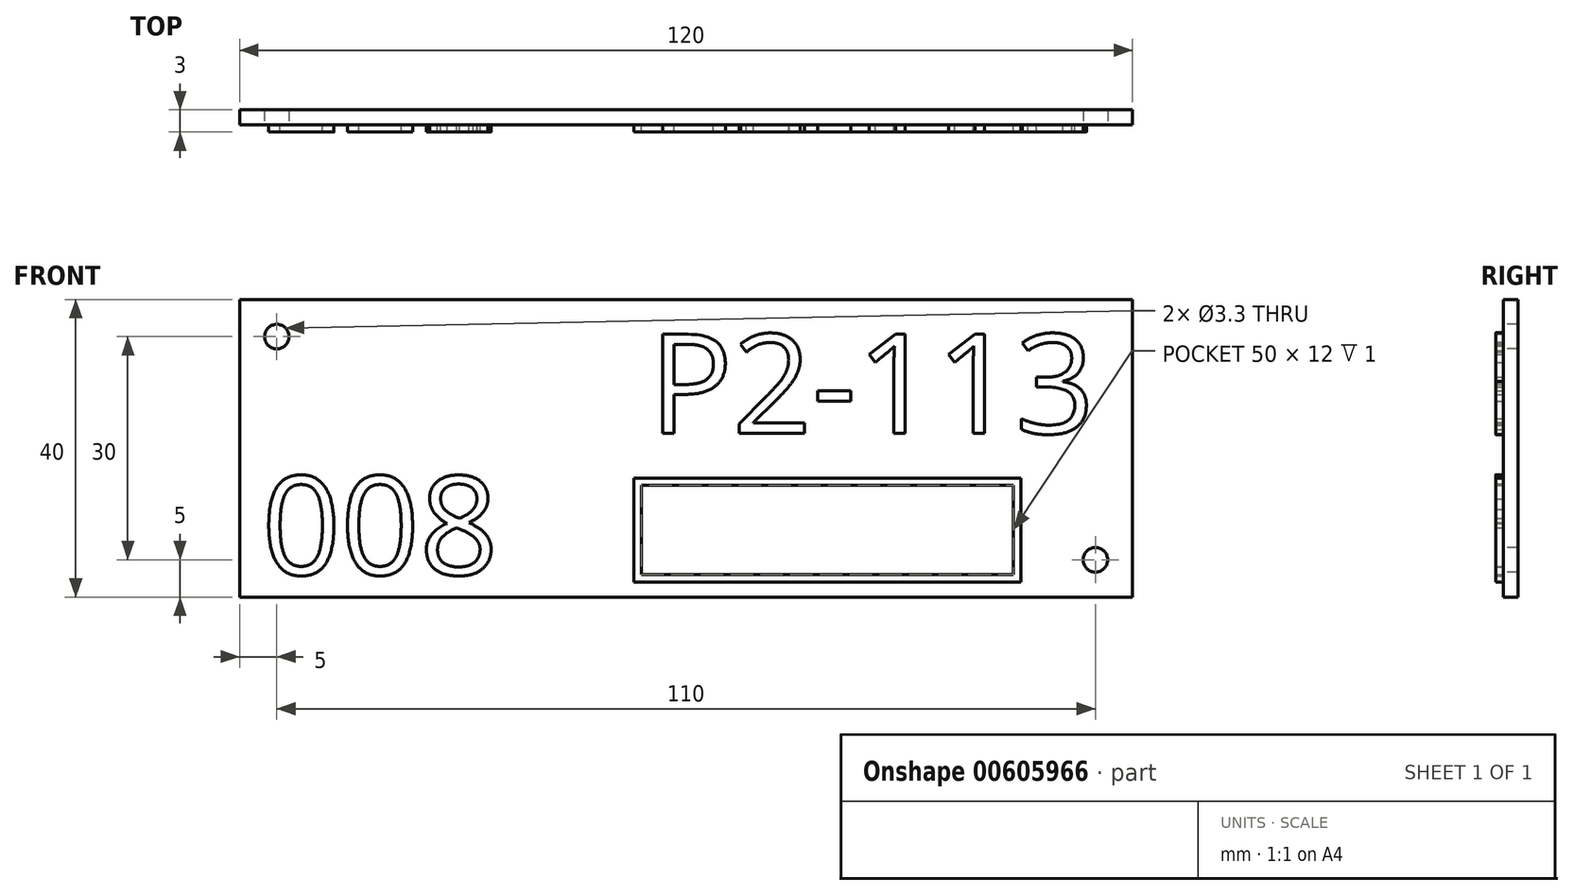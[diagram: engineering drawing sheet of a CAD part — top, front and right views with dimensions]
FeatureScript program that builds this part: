
annotation { "Feature Type Name" : "Feature", "Feature Type Description" : "" }
export const myFeature = defineFeature(function(context is Context, id is Id, definition is map)
    precondition{}
    {
        {
            var Q0;
            Q0=qCreatedBy(makeId("Front.planeOp"),FACE);
            var sketch = newSketch(context, id + "F0", { "sketchPlane" : qUnion([Q0])});
            skLineSegment(sketch, "E0.bottom", {"start": v(60, -20) * mm, "end": v(-60, -20) * mm});
            skLineSegment(sketch, "E0.top", {"start": v(60, 20) * mm, "end": v(-60, 20) * mm});
            skLineSegment(sketch, "E0.left", {"start": v(60, -20) * mm, "end": v(60, 20) * mm});
            skLineSegment(sketch, "E0.right", {"start": v(-60, -20) * mm, "end": v(-60, 20) * mm});
            skPoint(sketch, "E0.middle", {"position": v(0, 0) * mm});
            skSolve(sketch);
        }
        {
            var Q0;
            Q0=makeQuery(id+"F0.imprint","IMPRINT",FACE,{"disambiguationData":[TD([[makeQuery(id+"F0.imprint","IMPRINT",EDGE,{"derivedFrom":sQuery(id+"F0.wireOp",EDGE,"E0.bottom")}),-1.0]])]});
            extrude(context, id + "F1", {"entities" : qUnion([Q0]), "depth" : 2 * mm});
        }
        {
            var Q0;
            Q0=makeQuery(id+"F1.opExtrude","CAP_FACE",FACE,{"disambiguationData":[OSD([sQuery(id+"F0.wireOp",EDGE,"E0.bottom"),sQuery(id+"F0.wireOp",EDGE,"E0.top"),sQuery(id+"F0.wireOp",EDGE,"E0.left"),sQuery(id+"F0.wireOp",EDGE,"E0.right")])],"isStart":false});
            var sketch = newSketch(context, id + "F2", { "sketchPlane" : qUnion([Q0])});
            skPoint(sketch, "E1", {"position": v(-55, 15) * mm});
            skPoint(sketch, "E2", {"position": v(55, -15) * mm});
            skSolve(sketch);
        }
        {
            var Q0;
            Q0=sQuery(id+"F2.wireOp",VERTEX,"E1");
            var Q1;
            Q1=sQuery(id+"F2.wireOp",VERTEX,"E2");
            var Q2;
            Q2=makeQuery(id+"F1.opExtrude","SWEPT_BODY",BODY,{"disambiguationData":[OSD([sQuery(id+"F0.wireOp",EDGE,"E0.bottom"),sQuery(id+"F0.wireOp",EDGE,"E0.top"),sQuery(id+"F0.wireOp",EDGE,"E0.left"),sQuery(id+"F0.wireOp",EDGE,"E0.right")])]});
            hole(context, id + "F3", {"style" : HoleStyle.SIMPLE, "endStyle" : HoleEndStyle.THROUGH, "holeDiameter" : 3.3 * mm, "locations" : qUnion([Q0, Q1]), "scope" : qUnion([Q2]), "isTappedThrough" : true});
        }
        {
            var Q0;
            Q0=makeQuery(id+"F1.opExtrude","CAP_FACE",FACE,{"disambiguationData":[OSD([sQuery(id+"F0.wireOp",EDGE,"E0.bottom"),sQuery(id+"F0.wireOp",EDGE,"E0.top"),sQuery(id+"F0.wireOp",EDGE,"E0.left"),sQuery(id+"F0.wireOp",EDGE,"E0.right")])],"isStart":false});
            var sketch = newSketch(context, id + "F4", { "sketchPlane" : qUnion([Q0])});
            skText(sketch, "E3", { "text": "P2-113", "fontName": "OpenSans-Regular.ttf"});
            const initialGuessF4  = {"E3": [-0.005, 0.002, 1, 0, 0.01343]};
            skSetInitialGuess(sketch, initialGuessF4);
            skSolve(sketch);
        }
        {
            var Q0;
            Q0=qSketchRegion(id+"F4",true);
            extrude(context, id + "F5", {"entities" : qUnion([Q0]), "operationType" : NewBodyOperationType.ADD, "depth" : 1 * mm});
        }
        {
            var Q0;
            {var subQ0=sQuery(id+"F0.wireOp",EDGE,"E0.top");var subQ1=sQuery(id+"F0.wireOp",EDGE,"E0.left");var subQ2=sQuery(id+"F0.wireOp",EDGE,"E0.right");var subQ3=sQuery(id+"F0.wireOp",EDGE,"E0.bottom");Q0=makeQuery(id+"F5.boolean.opBoolean","SPLIT",FACE,{"disambiguationData":[TD([makeQuery(id+"F1.opExtrude","SWEPT_FACE",FACE,{"disambiguationData":[OSD([subQ3])]})])],"derivedFrom":makeQuery(id+"F1.opExtrude","CAP_FACE",FACE,{"disambiguationData":[OSD([subQ3,subQ0,subQ1,subQ2])],"isStart":false})});}
            var sketch = newSketch(context, id + "F6", { "sketchPlane" : qUnion([Q0])});
            skText(sketch, "E4", { "text": "008", "fontName": "OpenSans-Regular.ttf"});
            const initialGuessF6  = {"E4": [-0.057, -0.017, 1, 0, 0.01333]};
            skSetInitialGuess(sketch, initialGuessF6);
            skSolve(sketch);
        }
        {
            var Q0;
            Q0=qSketchRegion(id+"F6",true);
            extrude(context, id + "F7", {"entities" : qUnion([Q0]), "operationType" : NewBodyOperationType.ADD, "depth" : 1 * mm});
        }
        {
            var Q0;
            {var subQ46=sQuery(id+"F0.wireOp",EDGE,"E0.top");var subQ48=sQuery(id+"F0.wireOp",EDGE,"E0.left");var subQ66=sQuery(id+"F0.wireOp",EDGE,"E0.right");var subQ76=sQuery(id+"F0.wireOp",EDGE,"E0.bottom");var subQ77=makeQuery(id+"F1.opExtrude","SWEPT_FACE",FACE,{"disambiguationData":[OSD([subQ76])]});Q0=makeQuery(id+"F7.boolean.opBoolean","SPLIT",FACE,{"disambiguationData":[TD([subQ77])],"derivedFrom":makeQuery(id+"F5.boolean.opBoolean","SPLIT",FACE,{"disambiguationData":[TD([subQ77])],"derivedFrom":makeQuery(id+"F1.opExtrude","CAP_FACE",FACE,{"disambiguationData":[OSD([subQ76,subQ46,subQ48,subQ66])],"isStart":false})})});}
            var sketch = newSketch(context, id + "F8", { "sketchPlane" : qUnion([Q0])});
            skLineSegment(sketch, "E5.bottom", {"start": v(45, -18) * mm, "end": v(-7, -18) * mm});
            skLineSegment(sketch, "E5.top", {"start": v(45, -4) * mm, "end": v(-7, -4) * mm});
            skLineSegment(sketch, "E5.left", {"start": v(45, -18) * mm, "end": v(45, -4) * mm});
            skLineSegment(sketch, "E5.right", {"start": v(-7, -18) * mm, "end": v(-7, -4) * mm});
            skPoint(sketch, "E5.middle", {"position": v(19, -11) * mm});
            skLineSegment(sketch, "E6.0", {"start": v(44, -5) * mm, "end": v(-6, -5) * mm});
            skLineSegment(sketch, "E6.1", {"start": v(44, -17) * mm, "end": v(44, -5) * mm});
            skLineSegment(sketch, "E6.2", {"start": v(44, -17) * mm, "end": v(-6, -17) * mm});
            skLineSegment(sketch, "E6.3", {"start": v(-6, -17) * mm, "end": v(-6, -5) * mm});
            skSolve(sketch);
        }
        {
            var Q0;
            Q0=makeQuery(id+"F8.imprint","IMPRINT",FACE,{"disambiguationData":[TD([[makeQuery(id+"F8.imprint","IMPRINT",EDGE,{"derivedFrom":sQuery(id+"F8.wireOp",EDGE,"E5.bottom")}),-1.0]])]});
            extrude(context, id + "F9", {"entities" : qUnion([Q0]), "operationType" : NewBodyOperationType.ADD, "depth" : 1 * mm});
        }
    });
